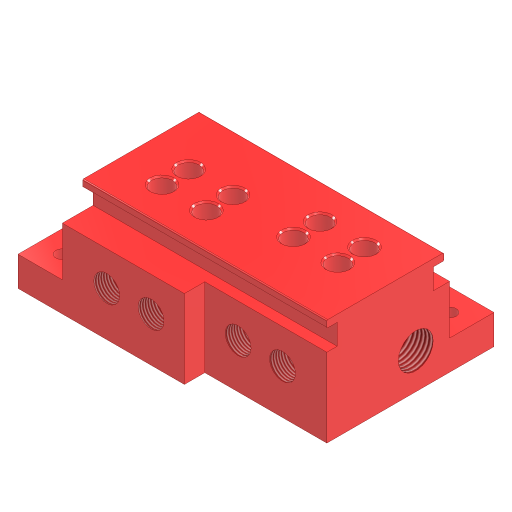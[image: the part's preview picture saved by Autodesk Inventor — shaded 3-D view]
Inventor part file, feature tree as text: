
AUTODESK INVENTOR PART (.ipt)
format: ipt  version: 2024.3 (Build 283343000, 343)  size: 372,736 bytes
history: native  units: mm
features: sketch x9, projected_geometry x8, extrude x7, direct_edit x3, move_body x3, hole x2, thread x2, fillet x1, chamfer x1, pattern_linear x1, plane x1, mirror x1
ambient origin geometry x8: Origin, YZ Plane, XZ Plane, XY Plane, X Axis, Y Axis, Z Axis, Center Point
bodies: Solid1 (feature_tree)
feature tree (39):
  extrude  "Extrusion1"  Depth=36.0mm
  extrude  "Extrusion2"  Depth=7.0mm
  hole  "Hole1"  [1 undecoded]
  fillet  "Fillet2"  [1 undecoded]
  chamfer  "Chamfer1"  Distance=2.0mm Angle=45.0deg
  direct_edit  "Direct Edit1"
  extrude  "Extrusion3"  Depth=2.0mm
  thread  "Thread1"  [1 undecoded]
  direct_edit  "Direct Edit2"
  extrude  "Extrusion4"  Depth=2.0mm TaperAngle=0.0deg
  extrude  "Extrusion5"  Depth=35.0mm TaperAngle=0.0deg
  thread  "Thread2"  [1 undecoded]
  pattern_linear  "Rectangular Pattern1"  Spacing1=0.0mm  [1 undecoded]
  plane  "Work Plane1"
  mirror  "Mirror1"
  direct_edit  "Direct Edit3"
  extrude  "Extrusion7"  Depth=2.0mm
  extrude  "Extrusion8"  Depth=2.0mm
  hole  "Hole3"  [1 undecoded]
  sketch  "Sketch1"  dims[d0=39.5mm d1=36.0mm]
  sketch  "Sketch2"  dims[d2=41.25mm d3=0.0mm d4=7.0mm]
  projected_geometry  "Projected Loop1"
  sketch  "Sketch4"  dims[d5=2.4mm d6=3.5mm d7=0.0mm d8=0.0mm]
  projected_geometry  "Projected Loop2"
  sketch  "Sketch5"  dims[d10=11.8mm]
  projected_geometry  "Projected Loop3"
  sketch  "Sketch7"  dims[d11=9.0mm]
  projected_geometry  "Projected Loop5"
  sketch  "Sketch8"  dims[d12=15.0mm]
  sketch  "Sketch10"  dims[d13=20.0mm d15=15.0mm d16=10.0mm d18=10.0mm]
  projected_geometry  "Projected Loop7"
  sketch  "Sketch11"  dims[d20=7.1mm d21=6.0mm d22=8.0mm d23=4.6mm d24=90.0deg d25=24.0mm d26=0.0mm]
  projected_geometry  "Projected Loop8"
  sketch  "Sketch13"  dims[d27=0.3mm d28=0.5mm d29=2.0mm d30=45.0deg d31=11.8mm d33=0.0mm d34=0.0mm d35=0.0mm d36=2.0mm d37=35.0mm d38=0.0mm d39=10.0mm d40=0.0mm d43=0.0mm d44=0.0mm d45=-3.0mm d46=7.1mm d47=6.0mm d48=18.7mm d49=0.0mm d50=8.8mm d51=13.0mm d52=0.0mm d53=12.0mm d54=0.0mm d55=20.0mm d57=15.0mm d58=0.0mm d59=-6.9mm d60=0.0mm d63=6.9mm d64=0.0mm d67=15.0mm d68=15.0mm d69=10.0mm d70=0.0mm d78=15.0mm d79=15.0mm d80=4.5mm d81=6.0mm d82=4.0mm d83=2.0mm d84=90.0deg d85=8.0mm d86=0.0mm d61=0.872665mm]
  projected_geometry  "Projected Loop11"
  projected_geometry  "Projected Loop12"
  move_body  "Move1"
  move_body  "Move2"
  move_body  "Move3"
note: 6 required parameter values undecoded (feature->parameter linkage not recoverable at this tier; creation-order binding heuristic only, values carry confidence <= 0.55)
